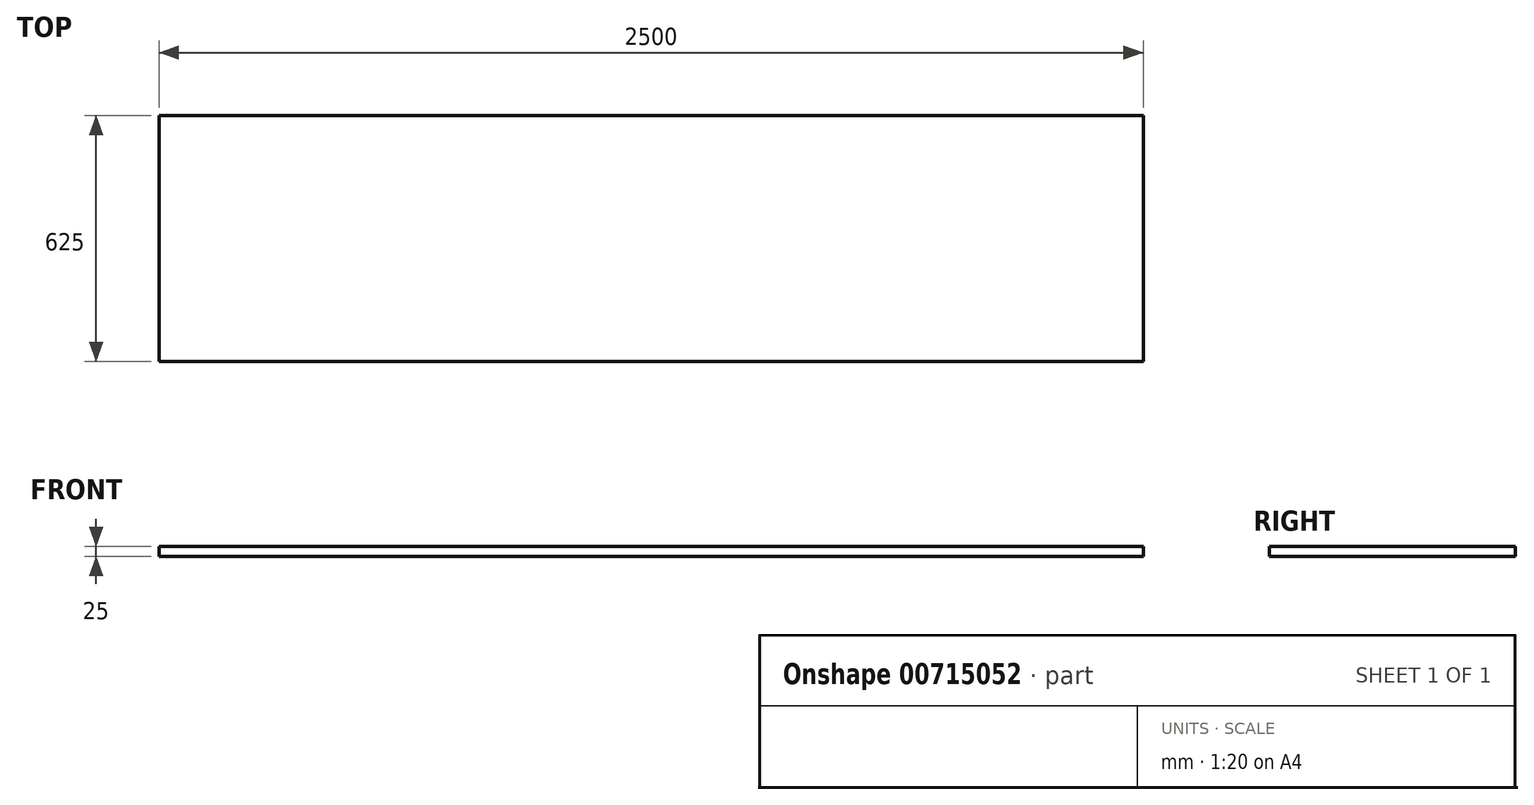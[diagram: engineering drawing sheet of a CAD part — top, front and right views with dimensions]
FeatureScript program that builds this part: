
annotation { "Feature Type Name" : "Feature", "Feature Type Description" : "" }
export const myFeature = defineFeature(function(context is Context, id is Id, definition is map)
    precondition{}
    {
        {
            var Q0;
            Q0=qCreatedBy(makeId("Top.planeOp"),FACE);
            var sketch = newSketch(context, id + "F0", { "sketchPlane" : qUnion([Q0])});
            skLineSegment(sketch, "E0.bottom", {"start": v(1250, 312.5) * mm, "end": v(-1250, 312.5) * mm});
            skLineSegment(sketch, "E0.top", {"start": v(1250, -312.5) * mm, "end": v(-1250, -312.5) * mm});
            skLineSegment(sketch, "E0.left", {"start": v(1250, 312.5) * mm, "end": v(1250, -312.5) * mm});
            skLineSegment(sketch, "E0.right", {"start": v(-1250, 312.5) * mm, "end": v(-1250, -312.5) * mm});
            skPoint(sketch, "E0.middle", {"position": v(0, 0) * mm});
            skSolve(sketch);
        }
        {
            var Q0;
            Q0=makeQuery(id+"F0.imprint","IMPRINT",FACE,{"disambiguationData":[TD([[makeQuery(id+"F0.imprint","IMPRINT",EDGE,{"derivedFrom":sQuery(id+"F0.wireOp",EDGE,"E0.bottom")}),1.0]])]});
            extrude(context, id + "F1", {"entities" : qUnion([Q0]), "depth" : 25 * mm, "offsetDistance" : 25 * mm});
        }
    });
